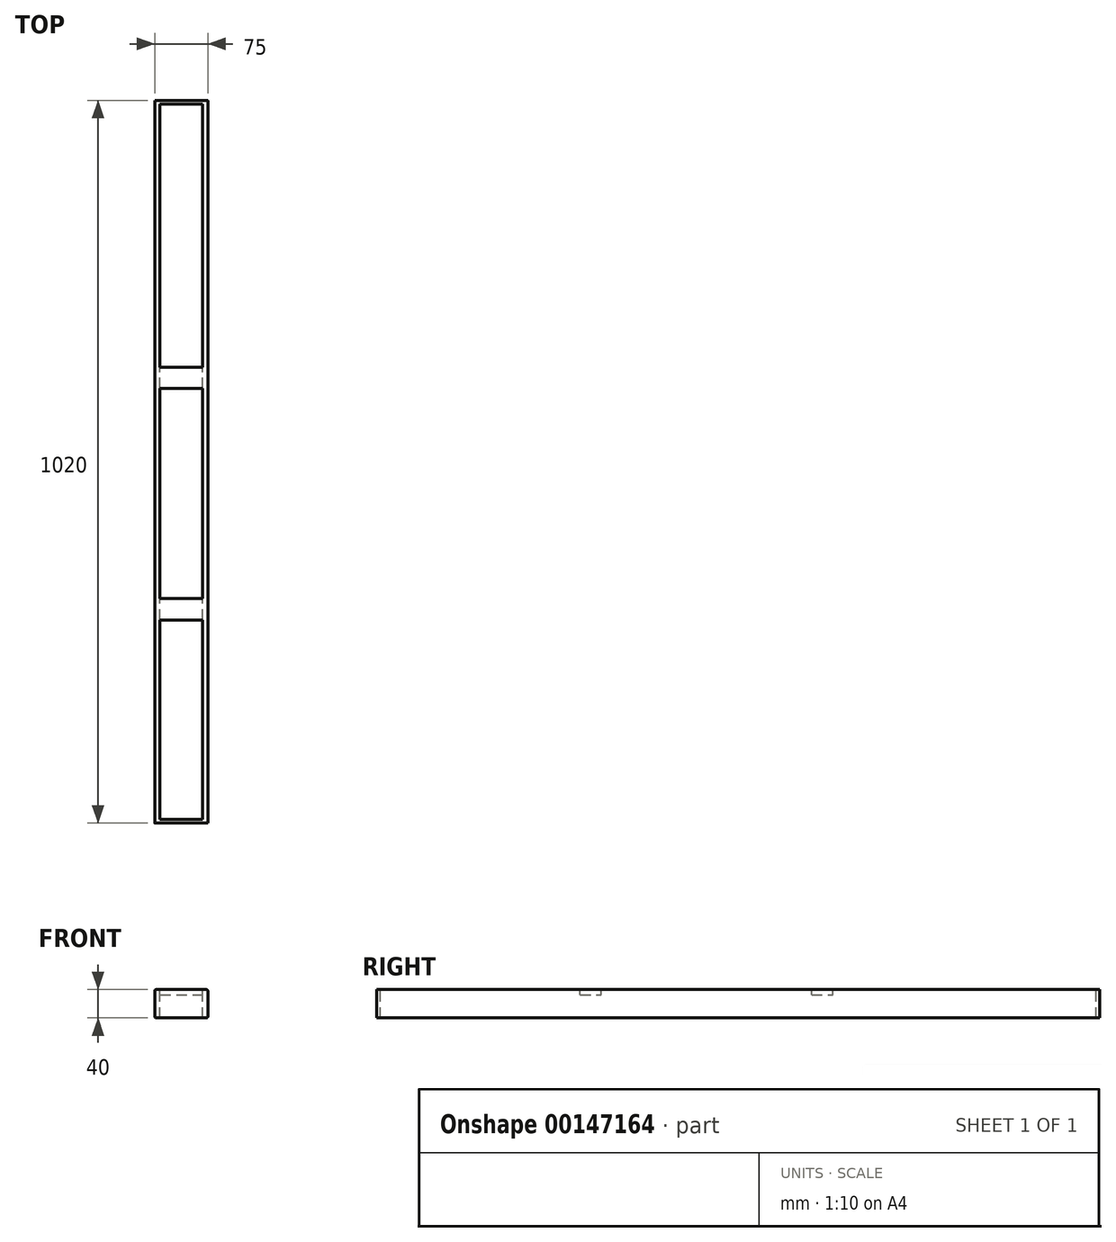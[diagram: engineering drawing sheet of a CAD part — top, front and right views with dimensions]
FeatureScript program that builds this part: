
annotation { "Feature Type Name" : "Feature", "Feature Type Description" : "" }
export const myFeature = defineFeature(function(context is Context, id is Id, definition is map)
    precondition{}
    {
        {
            var Q0;
            Q0=qCreatedBy(makeId("Front.planeOp"),FACE);
            var sketch = newSketch(context, id + "F0", { "sketchPlane" : qUnion([Q0])});
            skLineSegment(sketch, "E0.bottom", {"start": v(37.5, -20) * mm, "end": v(30, -20) * mm});
            skLineSegment(sketch, "E0.top", {"start": v(37.5, 20) * mm, "end": v(-37.5, 20) * mm});
            skLineSegment(sketch, "E0.left", {"start": v(37.5, -20) * mm, "end": v(37.5, 20) * mm});
            skLineSegment(sketch, "E0.right", {"start": v(-37.5, -20) * mm, "end": v(-37.5, 20) * mm});
            skPoint(sketch, "E0.middle", {"position": v(0, 0) * mm});
            skLineSegment(sketch, "E1.top", {"start": v(30, 12.5) * mm, "end": v(-30, 12.5) * mm});
            skLineSegment(sketch, "E1.left", {"start": v(30, -12.5) * mm, "end": v(30, 12.5) * mm});
            skLineSegment(sketch, "E1.right", {"start": v(-30, -12.5) * mm, "end": v(-30, 12.5) * mm});
            skLineSegment(sketch, "E2", {"start": v(-30, -12.5) * mm, "end": v(-30, -20) * mm});
            skLineSegment(sketch, "E3", {"start": v(30, -12.5) * mm, "end": v(30, -20) * mm});
            skLineSegment(sketch, "E4.trimOffspring", {"start": v(-30, -20) * mm, "end": v(-37.5, -20) * mm});
            skSolve(sketch);
        }
        {
            var Q0;
            Q0=makeQuery(id+"F0.imprint","IMPRINT",FACE,{"disambiguationData":[TD([[makeQuery(id+"F0.imprint","IMPRINT",EDGE,{"derivedFrom":sQuery(id+"F0.wireOp",EDGE,"E0.bottom")}),-1.0]])]});
            extrude(context, id + "F1", {"entities" : qUnion([Q0]), "depth" : 1020 * mm});
        }
        {
            var Q0;
            Q0=makeQuery(id+"F1.opExtrude","SWEPT_FACE",FACE,{"disambiguationData":[OSD([sQuery(id+"F0.wireOp",EDGE,"E0.top")])]});
            var sketch = newSketch(context, id + "F2", { "sketchPlane" : qUnion([Q0])});
            skLineSegment(sketch, "E5.bottom", {"start": v(30, -1015) * mm, "end": v(-30, -1015) * mm});
            skLineSegment(sketch, "E5.top", {"start": v(30, -733.17) * mm, "end": v(-30, -733.17) * mm});
            skLineSegment(sketch, "E5.left", {"start": v(30, -1015) * mm, "end": v(30, -733.17) * mm});
            skLineSegment(sketch, "E5.right", {"start": v(-30, -1015) * mm, "end": v(-30, -733.17) * mm});
            skLineSegment(sketch, "E6.bottom", {"start": v(30, -703.17) * mm, "end": v(-30, -703.17) * mm});
            skLineSegment(sketch, "E6.top", {"start": v(30, -406.34) * mm, "end": v(-30, -406.34) * mm});
            skLineSegment(sketch, "E6.left", {"start": v(30, -703.17) * mm, "end": v(30, -406.34) * mm});
            skLineSegment(sketch, "E6.right", {"start": v(-30, -703.17) * mm, "end": v(-30, -406.34) * mm});
            skLineSegment(sketch, "E7.bottom", {"start": v(30, -376.34) * mm, "end": v(-30, -376.34) * mm});
            skLineSegment(sketch, "E7.top", {"start": v(30, -5) * mm, "end": v(-30, -5) * mm});
            skLineSegment(sketch, "E7.left", {"start": v(30, -376.34) * mm, "end": v(30, -5) * mm});
            skLineSegment(sketch, "E7.right", {"start": v(-30, -376.34) * mm, "end": v(-30, -5) * mm});
            skPoint(sketch, "E8.middle", {"position": v(0.05, -26.06) * mm});
            skPoint(sketch, "E8.middle.positionSnap0", {"position": v(-37.45, -26.06) * mm});
            skPoint(sketch, "E8.centerSnap0", {"position": v(-37.45, -26.06) * mm});
            skSolve(sketch);
        }
        {
            var Q0;
            Q0=qSketchRegion(id+"F2",true);
            extrude(context, id + "F3", {"entities" : qUnion([Q0]), "operationType" : NewBodyOperationType.REMOVE, "oppositeDirection" : true, "depth" : 60 * mm});
        }
        {
            var Q0;
            {var subQ4=sQuery(id+"F0.wireOp",EDGE,"E1.top");Q0=makeQuery(id+"F3.boolean.opBoolean","SPLIT",FACE,{"disambiguationData":[TD([makeQuery(id+"F3.opExtrude","SWEPT_FACE",FACE,{"disambiguationData":[OSD([sQuery(id+"F2.wireOp",EDGE,"E7.top")])]})])],"derivedFrom":makeQuery(id+"F1.opExtrude","SWEPT_FACE",FACE,{"disambiguationData":[OSD([subQ4])]})});}
            var Q1;
            {var subQ4=sQuery(id+"F0.wireOp",EDGE,"E1.top");Q1=makeQuery(id+"F3.boolean.opBoolean","SPLIT",FACE,{"disambiguationData":[TD([makeQuery(id+"F3.opExtrude","SWEPT_FACE",FACE,{"disambiguationData":[OSD([sQuery(id+"F2.wireOp",EDGE,"E5.bottom")])]})])],"derivedFrom":makeQuery(id+"F1.opExtrude","SWEPT_FACE",FACE,{"disambiguationData":[OSD([subQ4])]})});}
            extrude(context, id + "F4", {"entities" : qUnion([Q0, Q1]), "operationType" : NewBodyOperationType.ADD, "depth" : 32.5 * mm});
        }
        {
            var Q0;
            Q0=makeQuery(id+"F1.opExtrude","SWEPT_EDGE",EDGE,{"disambiguationData":[OSD([sQuery(id+"F0.wireOp",EDGE,"E0.top"),sQuery(id+"F0.wireOp",EDGE,"E0.left")])]});
            var Q1;
            Q1=makeQuery(id+"F1.opExtrude","SWEPT_EDGE",EDGE,{"disambiguationData":[OSD([sQuery(id+"F0.wireOp",EDGE,"E0.top"),sQuery(id+"F0.wireOp",EDGE,"E0.right")])]});
            var Q2;
            Q2=makeQuery(id+"F1.opExtrude","SWEPT_EDGE",EDGE,{"disambiguationData":[OSD([sQuery(id+"F0.wireOp",EDGE,"E0.bottom"),sQuery(id+"F0.wireOp",EDGE,"E0.left")])]});
            var Q3;
            Q3=makeQuery(id+"F1.opExtrude","SWEPT_EDGE",EDGE,{"disambiguationData":[OSD([sQuery(id+"F0.wireOp",EDGE,"E0.right"),sQuery(id+"F0.wireOp",EDGE,"E4.trimOffspring")])]});
            fillet(context, id + "F5", {"entities" : qUnion([Q0, Q1, Q2, Q3]), "radius" : 2 * mm, "tangentPropagation" : true, "allowEdgeOverflow" : false});
        }
    });
